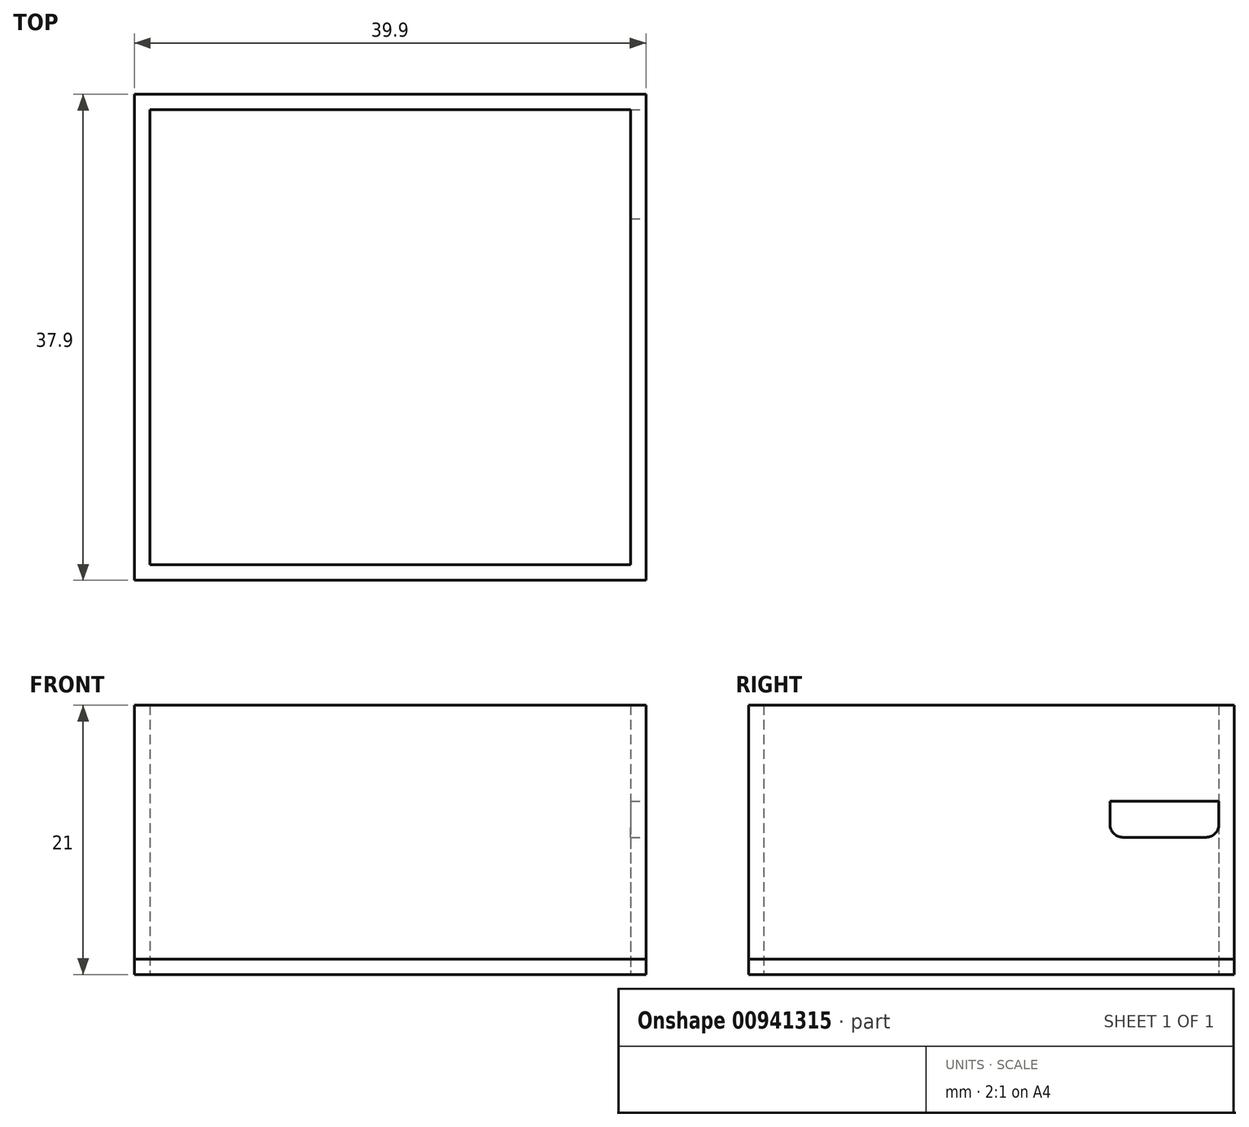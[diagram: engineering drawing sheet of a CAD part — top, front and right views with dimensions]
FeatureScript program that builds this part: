
annotation { "Feature Type Name" : "Feature", "Feature Type Description" : "" }
export const myFeature = defineFeature(function(context is Context, id is Id, definition is map)
    precondition{}
    {
        {
            var Q0;
            Q0=qCreatedBy(makeId("Top.planeOp"),FACE);
            var sketch = newSketch(context, id + "F0", { "sketchPlane" : qUnion([Q0])});
            skLineSegment(sketch, "E0.bottom", {"start": v(-17.5, 18.98) * mm, "end": v(20, 18.98) * mm});
            skLineSegment(sketch, "E0.top", {"start": v(-17.5, -16.52) * mm, "end": v(20, -16.52) * mm});
            skLineSegment(sketch, "E0.left", {"start": v(-17.5, 18.98) * mm, "end": v(-17.5, -16.52) * mm});
            skLineSegment(sketch, "E0.right", {"start": v(20, 18.98) * mm, "end": v(20, -16.52) * mm});
            skLineSegment(sketch, "E1.0", {"start": v(21.2, 20.18) * mm, "end": v(21.2, -17.72) * mm});
            skLineSegment(sketch, "E1.1", {"start": v(-18.7, 20.18) * mm, "end": v(21.2, 20.18) * mm});
            skLineSegment(sketch, "E1.2", {"start": v(-18.7, 20.18) * mm, "end": v(-18.7, -17.72) * mm});
            skLineSegment(sketch, "E1.3", {"start": v(-18.7, -17.72) * mm, "end": v(21.2, -17.72) * mm});
            skPoint(sketch, "E2.visualSharp", {"position": v(-18.7, -17.72) * mm});
            skLineSegment(sketch, "E2.filletArc", {"start": v(-18.7, -17.72) * mm, "end": v(-18.7, -17.72) * mm});
            skPoint(sketch, "E3.visualSharp", {"position": v(-18.7, 20.18) * mm});
            skLineSegment(sketch, "E3.filletArc", {"start": v(-18.7, 20.18) * mm, "end": v(-18.7, 20.18) * mm});
            skPoint(sketch, "E4.visualSharp", {"position": v(21.2, 20.18) * mm});
            skLineSegment(sketch, "E4.filletArc", {"start": v(21.2, 20.18) * mm, "end": v(21.2, 20.18) * mm});
            skPoint(sketch, "E5.visualSharp", {"position": v(21.2, -17.72) * mm});
            skLineSegment(sketch, "E5.filletArc", {"start": v(21.2, -17.72) * mm, "end": v(21.2, -17.72) * mm});
            skSolve(sketch);
        }
        {
            var Q0;
            Q0 = qSketchRegion(id + "F0", true);
            var Q1;
            Q1=makeQuery(id+"F0.imprint","IMPRINT",FACE,{"disambiguationData":[TD([[makeQuery(id+"F0.imprint","IMPRINT",EDGE,{"derivedFrom":sQuery(id+"F0.wireOp",EDGE,"E0.bottom")}),-1.0]])]});
            extrude(context, id + "F1", {"entities" : qUnion([Q0, Q1]), "depth" : 1.2 * mm, "offsetDistance" : 25 * mm});
        }
        {
            var Q0;
            Q0 = qSketchRegion(id + "F0", true);
            extrude(context, id + "F2", {"entities" : qUnion([Q0]), "depth" : 21 * mm, "offsetDistance" : 25 * mm});
        }
        {
            var Q0;
            Q0=makeQuery(id+"F2.opExtrude","SWEPT_FACE",FACE,{"disambiguationData":[OSD([sQuery(id+"F0.wireOp",EDGE,"E1.0")])]});
            var sketch = newSketch(context, id + "F3", { "sketchPlane" : qUnion([Q0])});
            skLineSegment(sketch, "E6.top", {"start": v(11.48, 10.7) * mm, "end": v(17.98, 10.7) * mm});
            skLineSegment(sketch, "E6.left", {"start": v(10.48, 13.5) * mm, "end": v(10.48, 11.7) * mm});
            skLineSegment(sketch, "E6.right", {"start": v(18.98, 13.5) * mm, "end": v(18.98, 11.7) * mm});
            skPoint(sketch, "E7.visualSharp", {"position": v(10.48, 10.7) * mm});
            skArc(sketch, "E7.filletArc", {"start": v(10.48, 11.7) * mm, "mid": v(10.78, 11) * mm, "end": v(11.48, 10.7) * mm});
            skPoint(sketch, "E8.visualSharp", {"position": v(18.98, 10.7) * mm});
            skArc(sketch, "E9.filletArc", {"start": v(17.98, 10.7) * mm, "mid": v(18.7, 11) * mm, "end": v(18.98, 11.7) * mm});
            skLineSegment(sketch, "E10", {"start": v(10.48, 13.5) * mm, "end": v(18.98, 13.5) * mm});
            skSolve(sketch);
        }
        {
            var Q0;
            Q0=makeQuery(id+"F3.imprint","IMPRINT",FACE,{"disambiguationData":[TD([[makeQuery(id+"F3.imprint","IMPRINT",EDGE,{"derivedFrom":sQuery(id+"F3.wireOp",EDGE,"E6.top")}),1.0]])]});
            extrude(context, id + "F4", {"entities" : qUnion([Q0]), "operationType" : NewBodyOperationType.REMOVE, "oppositeDirection" : true, "depth" : 2 * mm, "offsetDistance" : 25 * mm});
        }
    });
